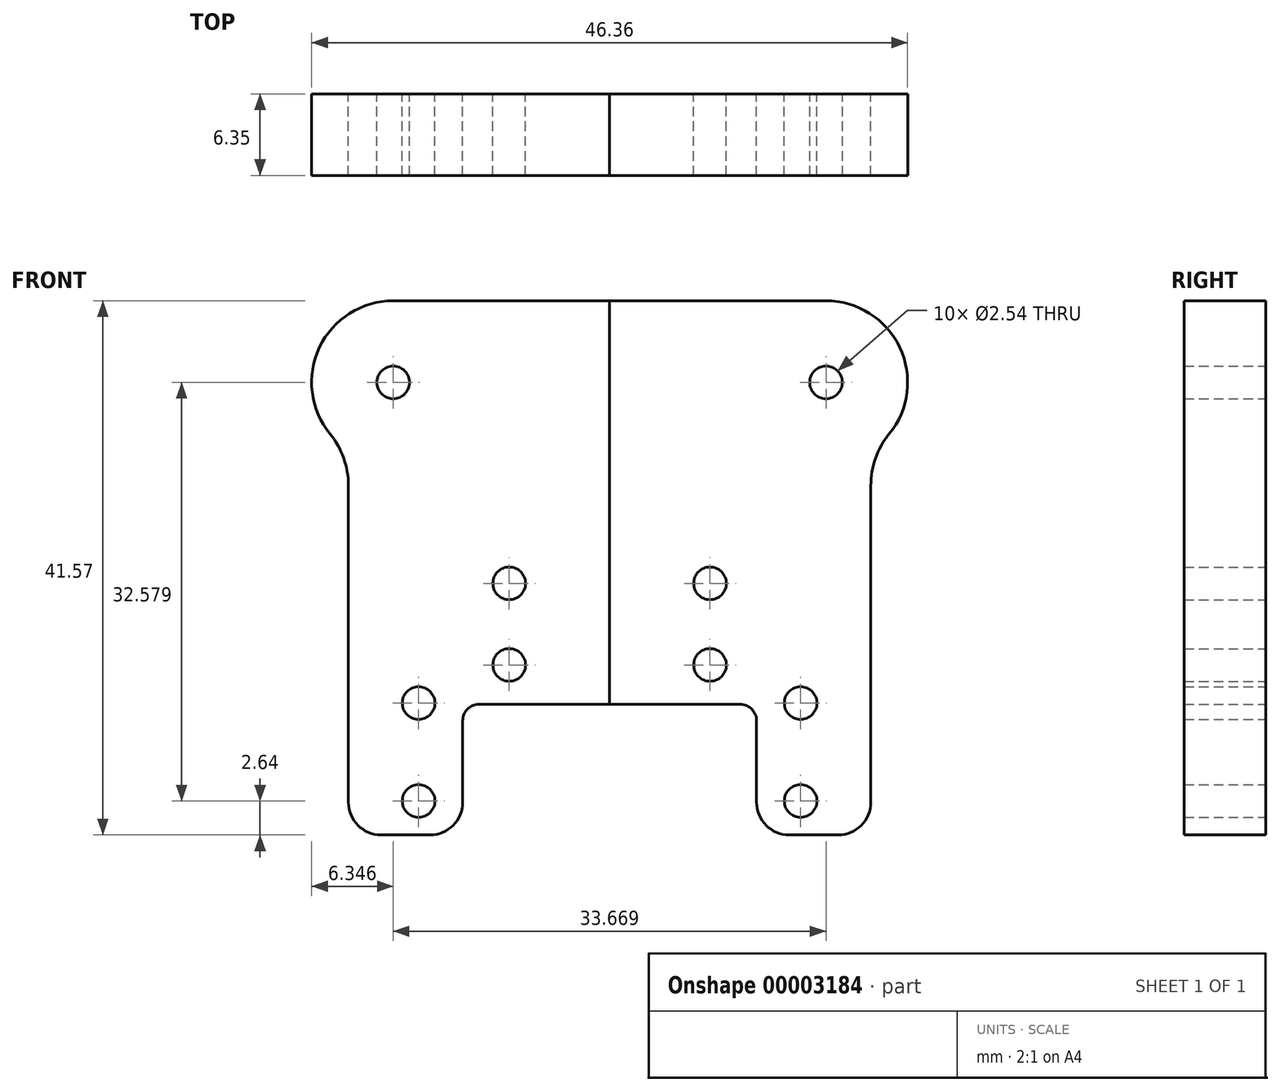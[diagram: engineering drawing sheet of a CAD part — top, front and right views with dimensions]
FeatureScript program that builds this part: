
annotation { "Feature Type Name" : "Feature", "Feature Type Description" : "" }
export const myFeature = defineFeature(function(context is Context, id is Id, definition is map)
    precondition{}
    {
        {
            var Q0;
            Q0=qCreatedBy(makeId("Front.planeOp"),FACE);
            var sketch = newSketch(context, id + "F0", { "sketchPlane" : qUnion([Q0])});
            skLineSegment(sketch, "E0", {"start": v(0, 0) * mm, "end": v(0, 35.2) * mm, "construction": true});
            skCircle(sketch, "E1", {"center": v(-14.86, -20.6) * mm, "radius": 1.27 * mm});
            skCircle(sketch, "E2", {"center": v(-7.81, -10.01) * mm, "radius": 1.27 * mm});
            skCircle(sketch, "E3", {"center": v(-7.81, -3.66) * mm, "radius": 1.27 * mm});
            skLineSegment(sketch, "E4", {"start": v(-7.81, -3.66) * mm, "end": v(-7.81, -10.01) * mm, "construction": true});
            skCircle(sketch, "E5", {"center": v(-14.86, -12.98) * mm, "radius": 1.27 * mm});
            skCircle(sketch, "E6", {"center": v(-16.83, 11.98) * mm, "radius": 1.27 * mm});
            skLineSegment(sketch, "E7", {"start": v(-11.43, -20.7) * mm, "end": v(-11.43, -13.08) * mm});
            skLineSegment(sketch, "E8", {"start": v(-11.43, -13.08) * mm, "end": v(0, -13.08) * mm});
            skLineSegment(sketch, "E9", {"start": v(-13.97, -23.24) * mm, "end": v(-17.78, -23.24) * mm});
            skLineSegment(sketch, "E10", {"start": v(-20.32, -20.7) * mm, "end": v(-20.32, 3.94) * mm});
            skLineSegment(sketch, "E11", {"start": v(-16.83, 18.33) * mm, "end": v(0, 18.33) * mm});
            skLineSegment(sketch, "E12", {"start": v(0, 18.33) * mm, "end": v(0, -13.08) * mm});
            skArc(sketch, "E13.filletArc", {"start": v(-16.83, 18.33) * mm, "mid": v(-22.57, 14.7) * mm, "end": v(-21.75, 7.96) * mm});
            skArc(sketch, "E14.filletArc", {"start": v(-20.32, 3.94) * mm, "mid": v(-20.69, 6.08) * mm, "end": v(-21.75, 7.96) * mm});
            skPoint(sketch, "E15.visualSharp", {"position": v(-20.32, -23.24) * mm});
            skArc(sketch, "E15.filletArc", {"start": v(-20.32, -20.7) * mm, "mid": v(-19.58, -22.5) * mm, "end": v(-17.78, -23.24) * mm});
            skPoint(sketch, "E16.visualSharp", {"position": v(-11.43, -23.24) * mm});
            skArc(sketch, "E16.filletArc", {"start": v(-13.97, -23.24) * mm, "mid": v(-12.17, -22.5) * mm, "end": v(-11.43, -20.7) * mm});
            skSolve(sketch);
        }
        {
            var Q0;
            Q0 = qSketchRegion(id + "F0", true);
            extrude(context, id + "F1", {"entities" : qUnion([Q0]), "depth" : 6.35 * mm});
        }
        {
            var Q0;
            Q0=makeQuery(id+"F1.opExtrude","SWEPT_BODY",BODY,{"disambiguationData":[OSD([sQuery(id+"F0.wireOp",EDGE,"E1"),sQuery(id+"F0.wireOp",EDGE,"E2"),sQuery(id+"F0.wireOp",EDGE,"E3"),sQuery(id+"F0.wireOp",EDGE,"E5"),sQuery(id+"F0.wireOp",EDGE,"E6"),sQuery(id+"F0.wireOp",EDGE,"E7"),sQuery(id+"F0.wireOp",EDGE,"E8"),sQuery(id+"F0.wireOp",EDGE,"E9"),sQuery(id+"F0.wireOp",EDGE,"E10"),sQuery(id+"F0.wireOp",EDGE,"0c2460cd-548c-4d79-9208-89ad9bdbc510"),sQuery(id+"F0.wireOp",EDGE,"12dd31ad-a5a0-4321-90ab-b31e6a9f6a9e"),sQuery(id+"F0.wireOp",EDGE,"E11"),sQuery(id+"F0.wireOp",EDGE,"E12"),sQuery(id+"F0.wireOp",EDGE,"E13.filletArc"),sQuery(id+"F0.wireOp",EDGE,"2987cfe4-d1f2-4717-b135-0c2b46f17b9e.filletArc"),sQuery(id+"F0.wireOp",EDGE,"E14.filletArc"),sQuery(id+"F0.wireOp",EDGE,"E15.filletArc"),sQuery(id+"F0.wireOp",EDGE,"E16.filletArc")])]});
            var Q1;
            Q1=qCreatedBy(makeId("Right.planeOp"),FACE);
            mirror(context, id + "F2", {"entities" : qUnion([Q0]), "mirrorPlane" : qUnion([Q1])});
        }
        {
            var Q0;
            Q0=makeQuery(id+"F1.opExtrude","SWEPT_EDGE",EDGE,{"disambiguationData":[OSD([sQuery(id+"F0.wireOp",EDGE,"E7"),sQuery(id+"F0.wireOp",EDGE,"E8")])]});
            var Q1;
            Q1=makeQuery(id+"F2.opPattern","COPY",EDGE,{"derivedFrom":makeQuery(id+"F1.opExtrude","SWEPT_EDGE",EDGE,{"disambiguationData":[OSD([sQuery(id+"F0.wireOp",EDGE,"E7"),sQuery(id+"F0.wireOp",EDGE,"E8")])]}),"instanceName":"1"});
            fillet(context, id + "F3", {"entities" : qUnion([Q0, Q1]), "radius" : 1.27 * mm, "tangentPropagation" : true, "allowEdgeOverflow" : false});
        }
    });
